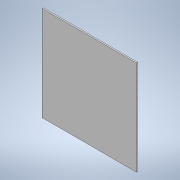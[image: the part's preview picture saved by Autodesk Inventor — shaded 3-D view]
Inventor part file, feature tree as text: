
AUTODESK INVENTOR PART (.ipt)
format: ipt  version: 2021 (Build 250183000, 183)  size: 89,088 bytes
history: native  units: in
note: dims shown in document units (in); Inventor stores cm internally (conversion verified against a paired STEP export)
features: extrude x1, sketch x1
ambient origin geometry x8: Origin, YZ Plane, XZ Plane, XY Plane, X Axis, Y Axis, Z Axis, Center Point
bodies: Solid1 (feature_tree)
feature tree (2):
  extrude  "Extrusion1"  Depth=3.0in
  sketch  "Sketch1"  dims[d0=3.0in d1=3.0in d2=0.0394in d3=0.0in]
